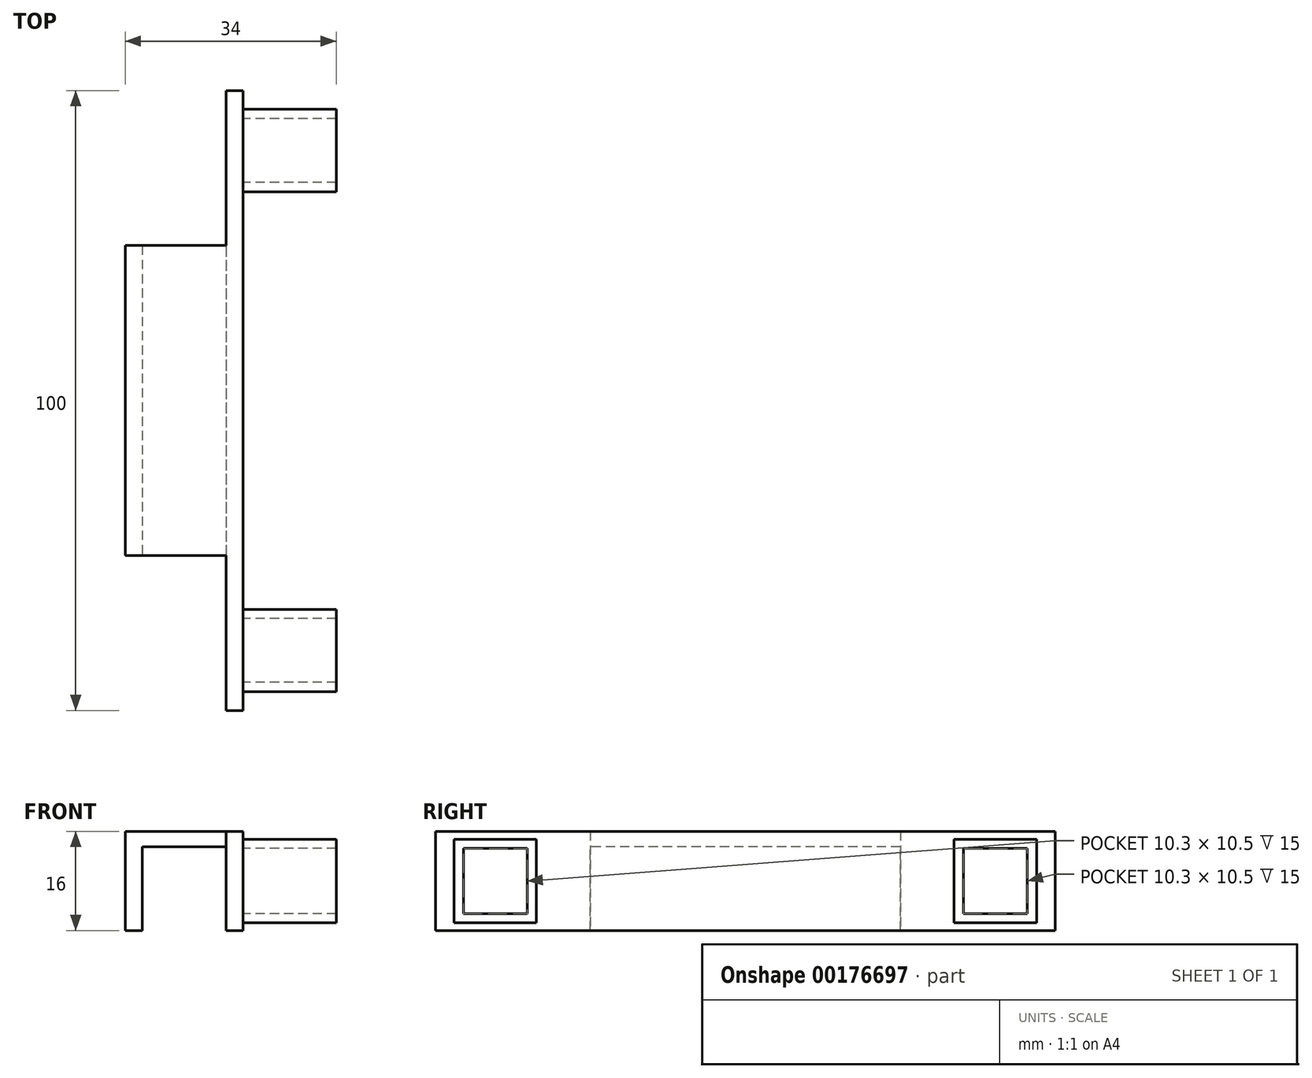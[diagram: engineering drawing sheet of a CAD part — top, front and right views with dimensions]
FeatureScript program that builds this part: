
annotation { "Feature Type Name" : "Feature", "Feature Type Description" : "" }
export const myFeature = defineFeature(function(context is Context, id is Id, definition is map)
    precondition{}
    {
        {
            var Q0;
            Q0=qCreatedBy(makeId("Top.planeOp"),FACE);
            var sketch = newSketch(context, id + "F0", { "sketchPlane" : qUnion([Q0])});
            skLineSegment(sketch, "E0.bottom", {"start": v(-9.5, 25) * mm, "end": v(9.5, 25) * mm});
            skLineSegment(sketch, "E0.top", {"start": v(-9.5, -25) * mm, "end": v(9.5, -25) * mm});
            skLineSegment(sketch, "E0.left", {"start": v(-9.5, 25) * mm, "end": v(-9.5, -25) * mm});
            skLineSegment(sketch, "E0.right", {"start": v(9.5, 25) * mm, "end": v(9.5, -25) * mm});
            skPoint(sketch, "E0.middle", {"position": v(0, 0) * mm});
            skSolve(sketch);
        }
        {
            var Q0;
            Q0 = qSketchRegion(id + "F0", true);
            extrude(context, id + "F1", {"entities" : qUnion([Q0]), "depth" : 16 * mm});
        }
        {
            var Q0;
            Q0=makeQuery(id+"F1.opExtrude","SWEPT_FACE",FACE,{"disambiguationData":[OSD([sQuery(id+"F0.wireOp",EDGE,"E0.top")])]});
            var sketch = newSketch(context, id + "F2", { "sketchPlane" : qUnion([Q0])});
            skLineSegment(sketch, "E1.bottom", {"start": v(-6.75, 0) * mm, "end": v(6.75, 0) * mm});
            skLineSegment(sketch, "E1.top", {"start": v(-6.75, 13.5) * mm, "end": v(6.75, 13.5) * mm});
            skLineSegment(sketch, "E1.left", {"start": v(-6.75, 0) * mm, "end": v(-6.75, 13.5) * mm});
            skLineSegment(sketch, "E1.right", {"start": v(6.75, 0) * mm, "end": v(6.75, 13.5) * mm});
            skSolve(sketch);
        }
        {
            var Q0;
            Q0=makeQuery(id+"F2.imprint","IMPRINT",FACE,{"disambiguationData":[TD([[makeQuery(id+"F2.imprint","IMPRINT",EDGE,{"derivedFrom":sQuery(id+"F2.wireOp",EDGE,"E1.bottom")}),1.0]])]});
            extrude(context, id + "F3", {"entities" : qUnion([Q0]), "operationType" : NewBodyOperationType.REMOVE, "oppositeDirection" : true, "depth" : 50 * mm});
        }
        {
            var Q0;
            Q0=makeQuery(id+"F1.opExtrude","SWEPT_FACE",FACE,{"disambiguationData":[OSD([sQuery(id+"F0.wireOp",EDGE,"E0.right")])]});
            var sketch = newSketch(context, id + "F4", { "sketchPlane" : qUnion([Q0])});
            skLineSegment(sketch, "E2.bottom", {"start": v(-50, 16) * mm, "end": v(50, 16) * mm});
            skLineSegment(sketch, "E2.top", {"start": v(-50, 0) * mm, "end": v(50, 0) * mm});
            skLineSegment(sketch, "E2.left", {"start": v(-50, 16) * mm, "end": v(-50, 0) * mm});
            skLineSegment(sketch, "E2.right", {"start": v(50, 16) * mm, "end": v(50, 0) * mm});
            skLineSegment(sketch, "E3.bottom", {"start": v(-45.49, 13.22) * mm, "end": v(-35.19, 13.22) * mm});
            skLineSegment(sketch, "E3.top", {"start": v(-45.49, 2.72) * mm, "end": v(-35.19, 2.72) * mm});
            skLineSegment(sketch, "E3.left", {"start": v(-45.49, 13.22) * mm, "end": v(-45.49, 2.72) * mm});
            skLineSegment(sketch, "E3.right", {"start": v(-35.19, 13.22) * mm, "end": v(-35.19, 2.72) * mm});
            skLineSegment(sketch, "E4.MirrorCS", {"start": v(35.19, 13.22) * mm, "end": v(35.19, 2.72) * mm});
            skLineSegment(sketch, "E5.MirrorCS", {"start": v(45.49, 2.72) * mm, "end": v(35.19, 2.72) * mm});
            skLineSegment(sketch, "E6.MirrorCS", {"start": v(45.49, 13.22) * mm, "end": v(35.19, 13.22) * mm});
            skLineSegment(sketch, "E7.MirrorCS", {"start": v(45.49, 13.22) * mm, "end": v(45.49, 2.72) * mm});
            skLineSegment(sketch, "E8.0", {"start": v(-46.99, 14.72) * mm, "end": v(-33.69, 14.72) * mm});
            skLineSegment(sketch, "E8.1", {"start": v(-46.99, 14.72) * mm, "end": v(-46.99, 1.22) * mm});
            skLineSegment(sketch, "E8.2", {"start": v(-46.99, 1.22) * mm, "end": v(-33.69, 1.22) * mm});
            skLineSegment(sketch, "E8.3", {"start": v(-33.69, 14.72) * mm, "end": v(-33.69, 1.22) * mm});
            skLineSegment(sketch, "E9.MirrorCS", {"start": v(33.69, 14.72) * mm, "end": v(33.69, 1.22) * mm});
            skLineSegment(sketch, "E10.MirrorCS", {"start": v(46.99, 1.22) * mm, "end": v(33.69, 1.22) * mm});
            skLineSegment(sketch, "E11.MirrorCS", {"start": v(46.99, 14.72) * mm, "end": v(33.69, 14.72) * mm});
            skLineSegment(sketch, "E12.MirrorCS", {"start": v(46.99, 14.72) * mm, "end": v(46.99, 1.22) * mm});
            skSolve(sketch);
        }
        {
            var Q0;
            Q0 = qSketchRegion(id + "F4", true);
            var Q1;
            Q1=makeQuery(id+"F4.imprint","IMPRINT",FACE,{"disambiguationData":[TD([[makeQuery(id+"F4.imprint","IMPRINT",EDGE,{"derivedFrom":sQuery(id+"F4.wireOp",EDGE,"E3.bottom")}),-1.0]])]});
            var Q2;
            Q2=makeQuery(id+"F4.imprint","IMPRINT",FACE,{"disambiguationData":[TD([[makeQuery(id+"F4.imprint","IMPRINT",EDGE,{"derivedFrom":sQuery(id+"F4.wireOp",EDGE,"E3.bottom")}),1.0]])]});
            var Q3;
            Q3=makeQuery(id+"F4.imprint","IMPRINT",FACE,{"disambiguationData":[TD([[makeQuery(id+"F4.imprint","IMPRINT",EDGE,{"derivedFrom":sQuery(id+"F4.wireOp",EDGE,"E4.MirrorCS")}),-1.0]])]});
            var Q4;
            Q4=makeQuery(id+"F4.imprint","IMPRINT",FACE,{"disambiguationData":[TD([[makeQuery(id+"F4.imprint","IMPRINT",EDGE,{"derivedFrom":sQuery(id+"F4.wireOp",EDGE,"E4.MirrorCS")}),1.0]])]});
            extrude(context, id + "F5", {"entities" : qUnion([Q0, Q1, Q2, Q3, Q4]), "operationType" : NewBodyOperationType.ADD, "oppositeDirection" : true, "depth" : 2.75 * mm});
        }
        {
            var Q0;
            Q0=makeQuery(id+"F4.imprint","IMPRINT",FACE,{"disambiguationData":[TD([[makeQuery(id+"F4.imprint","IMPRINT",EDGE,{"derivedFrom":sQuery(id+"F4.wireOp",EDGE,"E3.bottom")}),1.0]])]});
            var Q1;
            Q1=makeQuery(id+"F4.imprint","IMPRINT",FACE,{"disambiguationData":[TD([[makeQuery(id+"F4.imprint","IMPRINT",EDGE,{"derivedFrom":sQuery(id+"F4.wireOp",EDGE,"E4.MirrorCS")}),-1.0]])]});
            extrude(context, id + "F6", {"entities" : qUnion([Q0, Q1]), "operationType" : NewBodyOperationType.ADD, "depth" : 15 * mm});
        }
    });
